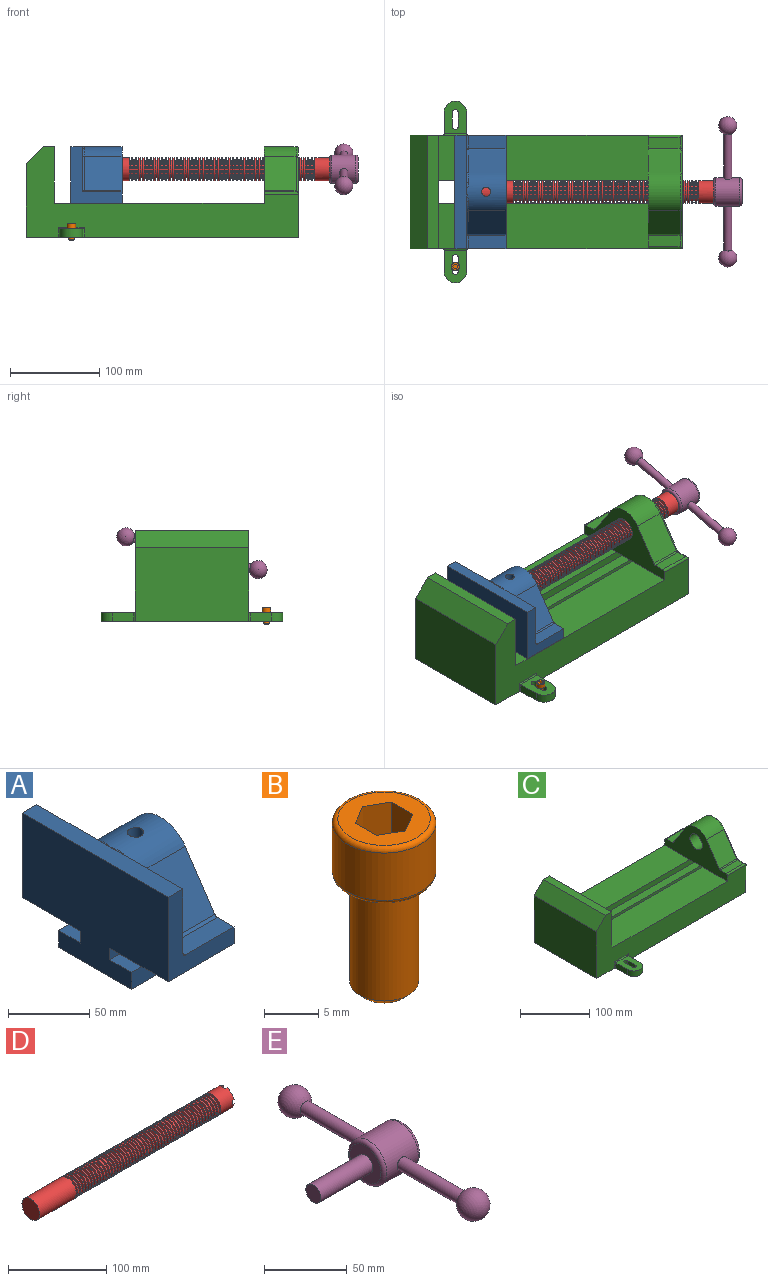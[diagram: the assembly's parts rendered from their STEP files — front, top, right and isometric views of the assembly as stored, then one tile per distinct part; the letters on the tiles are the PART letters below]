
ASSEMBLY  parts=5 mates=5
PART A: 36 faces, bbox 57.2x127x89 mm
  f0: plane 57.15x50.8mm, normal (0,0,-1), area 2903.2mm2, adj f6,f9,f10,f23
  f1: cylinder r=12.7mm len=44.45mm, axis (1,0,0), area 3464.3mm2, adj f6,f15,f16
  f2: plane 41.91x14.52mm, normal (0,0,1), area 608.5mm2, adj f6,f11,f24,f25
  f3: plane 51.86x48.26mm, normal (1,0,0), area 1495.7mm2, adj f8,f10,f31,f33,f35
  f4: plane 51.86x48.26mm, normal (1,0,0), area 1495.7mm2, adj f8,f11,f24,f28,f29
  f5: plane 57.15x50.8mm, normal (0,0,-1), area 2903.2mm2, adj f6,f9,f11,f22
  f6: plane 127x85.09mm, normal (1,0,0), area 5190.6mm2, adj f0,f1,f2,f5,f7,f10,f11,f12
  f7: plane 41.91x14.52mm, normal (0,0,1), area 608.5mm2, adj f6,f10,f30,f31
  f8: plane 127x12.7mm, normal (0,0,1), area 1612.9mm2, adj f3,f4,f9,f10,f11,f26,f34
  f9: plane 127x85.09mm, normal (-1,0,0), area 9096.8mm2, adj f0,f5,f8,f10,f11,f17,f18,f19
  f10: plane 63.5x57.15mm, normal (0,-1,0), area 1372.3mm2, adj f0,f3,f6,f7,f8,f9,f31
  f11: plane 63.5x57.15mm, normal (0,1,0), area 1372.3mm2, adj f2,f4,f5,f6,f8,f9,f24
  f12: plane 41.91x38.43mm, normal (0,-0.83,0.56), area 1939.2mm2, adj f6,f13,f30,f33
  f13: cylinder r=25.4mm len=44.45mm, axis (1,0,0), area 2026.5mm2, adj f6,f12,f14,f16,f26,f28,f34,f35
  f14: plane 41.91x38.43mm, normal (0,0.83,0.56), area 1939.2mm2, adj f6,f13,f25,f29
  f15: plane 25.4x25.4mm, normal (1,0,0), area 506.7mm2, adj f1
  f16: cylinder r=5.08mm len=13.76mm, axis (0,0,1), area 414mm2, adj f1,f13
  f17: plane 57.15x19.05mm, normal (0,0,1), area 1088.7mm2, adj f6,f9,f18,f23
  f18: plane 57.15x12.7mm, normal (0,-1,0), area 725.8mm2, adj f6,f9,f17,f19
  f19: plane 63.5x57.15mm, normal (0,0,-1), area 3629mm2, adj f6,f9,f18,f20
  f20: plane 57.15x12.7mm, normal (0,1,0), area 725.8mm2, adj f6,f9,f19,f21
  f21: plane 57.15x19.05mm, normal (0,0,1), area 1088.7mm2, adj f6,f9,f20,f22
  f22: plane 57.15x8.89mm, normal (0,1,0), area 508.1mm2, adj f5,f6,f9,f21
  f23: plane 57.15x8.89mm, normal (0,-1,0), area 508.1mm2, adj f0,f6,f9,f17
  f24: cylinder r=2.54mm len=14.52mm, axis (0,-1,0), area 57.9mm2, adj f2,f4,f11,f27
  f25: cylinder r=2.54mm len=41.91mm, axis (1,0,0), area 104.3mm2, adj f2,f6,f14,f27
  f26: bspline ~12.24x2.8mm, area 20.9mm2, adj f8,f13,f28
  f27: sphere r=2.54mm, area 6.3mm2, adj f24,f25,f29
  f28: torus R=27.94mm, axis (1,0,0), area 57.8mm2, adj f4,f13,f26,f29
  f29: cylinder r=2.54mm len=39.84mm, axis (0,-0.56,0.83), area 184.6mm2, adj f4,f14,f27,f28
  f30: cylinder r=2.54mm len=41.91mm, axis (1,0,0), area 104.3mm2, adj f6,f7,f12,f32
  f31: cylinder r=2.54mm len=14.52mm, axis (0,-1,0), area 57.9mm2, adj f3,f7,f10,f32
  f32: sphere r=2.54mm, area 6.3mm2, adj f30,f31,f33
  f33: cylinder r=2.54mm len=39.84mm, axis (0,-0.56,-0.83), area 184.6mm2, adj f3,f12,f32,f35
  f34: bspline ~12.24x2.8mm, area 20.9mm2, adj f8,f13,f35
  f35: torus R=27.94mm, axis (1,0,0), area 57.8mm2, adj f3,f13,f33,f34
PART B: 15 faces, bbox 10.3x10.3x19.1 mm
  f0: plane 8.51x8.51mm, normal (0,0,1), area 37.2mm2, adj f5,f6,f7,f8,f9,f10,f14
  f1: cylinder r=3.17mm len=11.94mm, axis (0,0,1), area 238.2mm2, adj f4,f12
  f2: plane 4.83x4.83mm, normal (0,0,-1), area 18.3mm2, adj f12
  f3: cylinder r=4.76mm len=9.53mm, axis (0,0,-1), area 159.6mm2, adj f13,f14
  f4: plane 8.51x8.51mm, normal (0,0,-1), area 25.2mm2, adj f1,f13
  f5: plane 4.83x2.38mm, normal (-0.5,-0.87,0), area 13.3mm2, adj f0,f6,f10,f11
  f6: plane 4.83x2.38mm, normal (0.5,-0.87,0), area 13.3mm2, adj f0,f5,f7,f11
  f7: plane 4.83x2.75mm, normal (1,0,0), area 13.3mm2, adj f0,f6,f8,f11
  f8: plane 4.83x2.38mm, normal (0.5,0.87,0), area 13.3mm2, adj f0,f7,f9,f11
  f9: plane 4.83x2.38mm, normal (-0.5,0.87,0), area 13.3mm2, adj f0,f8,f10,f11
  f10: plane 4.83x2.75mm, normal (-1,0,0), area 13.3mm2, adj f0,f5,f9,f11
  f11: plane 5.5x4.76mm, normal (0,0,1), area 19.6mm2, adj f5,f6,f7,f8,f9,f10
  f12: cone r=3.17mm half-angle=45deg, axis (0,0,1), area 18.9mm2, adj f1,f2
  f13: torus R=4.25mm, axis (0,0,1), area 23mm2, adj f3,f4
  f14: torus R=4.25mm, axis (0,0,1), area 23mm2, adj f0,f3
PART C: 61 faces, bbox 304.8x203.2x103.7 mm
  f0: plane 304.8x101.6mm, normal (0,1,0), area 13520.3mm2, adj f3,f4,f5,f6,f7,f8,f9,f16
  f1: plane 304.8x101.6mm, normal (0,-1,0), area 13520.3mm2, adj f2,f3,f5,f6,f7,f8,f9,f16
  f2: plane 234.95x50.8mm, normal (0,0,1), area 11935.5mm2, adj f1,f5,f16,f26
  f3: plane 127x99.06mm, normal (1,0,0), area 7097.5mm2, adj f0,f1,f9,f14,f17,f18,f19,f20
  f4: plane 234.95x50.8mm, normal (0,0,1), area 11935.5mm2, adj f0,f5,f16,f27
  f5: plane 127x101.6mm, normal (1,0,0), area 9516.1mm2, adj f0,f1,f2,f4,f6,f9,f18,f19
  f6: plane 127x12.7mm, normal (0,0,1), area 1612.9mm2, adj f0,f1,f5,f7
  f7: plane 127x19.05mm, normal (-0.71,0,0.71), area 3421.5mm2, adj f0,f1,f6,f8
  f8: plane 127x82.55mm, normal (-1,0,0), area 10483.8mm2, adj f0,f1,f7,f9
  f9: plane 304.8x203.2mm, normal (0,0,-1), area 33298.3mm2, adj f0,f1,f3,f5,f8,f21,f22,f39
  f10: plane 35.56x11.98mm, normal (0,0,1), area 426mm2, adj f16,f28,f29,f30
  f11: plane 38.43x35.56mm, normal (0,0.83,0.56), area 1645.4mm2, adj f12,f16,f29,f32
  f12: cylinder r=25.4mm len=42.19mm, axis (1,0,0), area 1770.2mm2, adj f11,f13,f16,f33
  f13: plane 38.43x35.56mm, normal (0,-0.83,0.56), area 1645.4mm2, adj f12,f16,f34,f35
  f14: cylinder r=12.7mm len=38.1mm, axis (1,0,0), area 3040.2mm2, adj f3,f16
  f15: plane 35.56x11.98mm, normal (0,0,1), area 426mm2, adj f16,f34,f36,f38
  f16: plane 127x63.5mm, normal (-1,0,0), area 4155.5mm2, adj f0,f1,f2,f4,f10,f11,f12,f13
  f17: plane 38.1x25.4mm, normal (0,0,-1), area 967.7mm2, adj f3,f16,f26,f27
  f18: plane 273.05x19.05mm, normal (0,0,-1), area 5201.6mm2, adj f3,f5,f19,f26
  f19: plane 273.05x12.7mm, normal (0,1,0), area 3467.7mm2, adj f3,f5,f18,f20
  f20: plane 273.05x19.05mm, normal (0,0,1), area 5201.6mm2, adj f3,f5,f19,f21
  f21: plane 273.05x16.51mm, normal (0,1,0), area 4508.1mm2, adj f3,f5,f9,f20
  f22: plane 273.05x16.51mm, normal (0,-1,0), area 4508.1mm2, adj f3,f5,f9,f23
  f23: plane 273.05x19.05mm, normal (0,0,1), area 5201.6mm2, adj f3,f5,f22,f24
  f24: plane 273.05x12.7mm, normal (0,-1,0), area 3467.7mm2, adj f3,f5,f23,f25
  f25: plane 273.05x19.05mm, normal (0,0,-1), area 5201.6mm2, adj f3,f5,f24,f27
  f26: plane 273.05x8.89mm, normal (0,1,0), area 2427.4mm2, adj f2,f3,f5,f17,f18
  f27: plane 273.05x8.89mm, normal (0,-1,0), area 2427.4mm2, adj f3,f4,f5,f17,f25
  f28: cylinder r=2.54mm len=38.1mm, axis (1,0,0), area 148.3mm2, adj f0,f10,f16,f30
  f29: cylinder r=2.54mm len=35.56mm, axis (-1,0,0), area 88.5mm2, adj f10,f11,f16,f31
  f30: cylinder r=2.54mm len=14.52mm, axis (0,1,0), area 54.3mm2, adj f3,f10,f28,f31
  f31: torus R=5.08mm, axis (-1,0,0), area 13.5mm2, adj f3,f29,f30,f32
  f32: cylinder r=2.54mm len=39.84mm, axis (0,0.56,-0.83), area 184.6mm2, adj f3,f11,f31,f33
  f33: torus R=22.86mm, axis (-1,0,0), area 191.4mm2, adj f3,f12,f32,f35
  f34: cylinder r=2.54mm len=35.56mm, axis (-1,0,0), area 88.5mm2, adj f13,f15,f16,f37
  f35: cylinder r=2.54mm len=39.84mm, axis (0,0.56,0.83), area 184.6mm2, adj f3,f13,f33,f37
  f36: cylinder r=2.54mm len=38.1mm, axis (-1,0,0), area 148.3mm2, adj f1,f15,f16,f38
  f37: torus R=5.08mm, axis (-1,0,0), area 13.5mm2, adj f3,f34,f35,f38
  f38: cylinder r=2.54mm len=14.52mm, axis (0,1,0), area 54.3mm2, adj f3,f15,f36,f37
  f39: plane 23.88x9.53mm, normal (-1,0,0), area 227.4mm2, adj f9,f45,f46,f60
  f40: plane 23.88x9.53mm, normal (1,0,0), area 227.4mm2, adj f9,f45,f46,f58
  f41: cylinder r=3.3mm len=9.53mm, axis (0,0,-1), area 98.8mm2, adj f9,f42,f44,f46
  f42: plane 15.62x9.53mm, normal (-1,0,0), area 148.8mm2, adj f9,f41,f43,f46
  f43: cylinder r=3.3mm len=9.53mm, axis (0,0,-1), area 98.8mm2, adj f9,f42,f44,f46
  f44: plane 15.62x9.53mm, normal (1,0,0), area 148.8mm2, adj f9,f41,f43,f46
  f45: cylinder r=12.7mm len=25.4mm, axis (0,0,-1), area 380mm2, adj f9,f39,f40,f46
  f46: plane 36.58x25.4mm, normal (0,0,1), area 722.4mm2, adj f39,f40,f41,f42,f43,f44,f45,f59
  f47: plane 23.88x9.53mm, normal (-1,0,0), area 227.4mm2, adj f9,f53,f54,f56
  f48: plane 23.88x9.53mm, normal (1,0,0), area 227.4mm2, adj f9,f53,f54,f55
  f49: cylinder r=3.3mm len=9.53mm, axis (0,0,-1), area 98.8mm2, adj f9,f50,f52,f54
  f50: plane 15.62x9.53mm, normal (-1,0,0), area 148.8mm2, adj f9,f49,f51,f54
  f51: cylinder r=3.3mm len=9.53mm, axis (0,0,-1), area 98.8mm2, adj f9,f50,f52,f54
  f52: plane 15.62x9.53mm, normal (1,0,0), area 148.8mm2, adj f9,f49,f51,f54
  f53: cylinder r=12.7mm len=25.4mm, axis (0,0,-1), area 380mm2, adj f9,f47,f48,f54
  f54: plane 36.58x25.4mm, normal (0,0,1), area 722.4mm2, adj f47,f48,f49,f50,f51,f52,f53,f57
  f55: cylinder r=1.52mm len=11.05mm, axis (0,0,-1), area 24.1mm2, adj f0,f9,f48,f57
  f56: cylinder r=1.52mm len=11.05mm, axis (0,0,1), area 24.1mm2, adj f0,f9,f47,f57
  f57: cylinder r=1.52mm len=28.45mm, axis (1,0,0), area 63.5mm2, adj f0,f54,f55,f56
  f58: cylinder r=1.52mm len=11.05mm, axis (0,0,1), area 24.1mm2, adj f1,f9,f40,f59
  f59: cylinder r=1.52mm len=28.45mm, axis (-1,0,0), area 63.5mm2, adj f1,f46,f58,f60
  f60: cylinder r=1.52mm len=11.05mm, axis (0,0,-1), area 24.1mm2, adj f1,f9,f39,f59
PART D: 220 faces, bbox 279.4x25.4x25.4 mm
  f0: cylinder r=12.7mm len=25.4mm, axis (-1,0,0), area 1468.2mm2, adj f1,f2,f3,f5,f7,f208,f209,f210
  f1: plane 9.9x9.9mm, normal (1,0,0), area 62.3mm2, adj f0,f4,f213,f216
  f2: plane 9.9x9.9mm, normal (1,0,0), area 62.3mm2, adj f0,f4,f210,f218
  f3: plane 9.9x9.9mm, normal (1,0,0), area 62.3mm2, adj f0,f4,f209,f212
  f4: cylinder r=6.35mm len=25.4mm, axis (1,0,0), area 960.3mm2, adj f1,f2,f3,f5,f6,f208,f209,f210
  f5: plane 9.9x9.9mm, normal (1,0,0), area 62.3mm2, adj f0,f4,f215,f217
  f6: plane 12.7x12.7mm, normal (1,0,0), area 126.7mm2, adj f4
  f7: cone r=12.7mm half-angle=76deg, axis (1,0,0), area 188mm2, adj f0,f9
  f8: cone r=10.16mm half-angle=76deg, axis (-1,0,0), area 188mm2, adj f9,f10
  f9: cylinder r=10.16mm len=20.32mm, axis (1,0,0), area 81.1mm2, adj f7,f8
  f10: cylinder r=12.7mm len=25.4mm, axis (-1,0,0), area 131.7mm2, adj f8,f11
  f11: cone r=12.7mm half-angle=76deg, axis (1,0,0), area 188mm2, adj f10,f13
  f12: cone r=10.16mm half-angle=76deg, axis (-1,0,0), area 188mm2, adj f13,f14
  f13: cylinder r=10.16mm len=20.32mm, axis (1,0,0), area 81.1mm2, adj f11,f12
  f14: cylinder r=12.7mm len=25.4mm, axis (-1,0,0), area 131.7mm2, adj f12,f15
  f15: cone r=12.7mm half-angle=76deg, axis (1,0,0), area 188mm2, adj f14,f17
  f16: cone r=10.16mm half-angle=76deg, axis (-1,0,0), area 188mm2, adj f17,f18
  f17: cylinder r=10.16mm len=20.32mm, axis (1,0,0), area 81.1mm2, adj f15,f16
  f18: cylinder r=12.7mm len=25.4mm, axis (-1,0,0), area 131.7mm2, adj f16,f19
  f19: cone r=12.7mm half-angle=76deg, axis (1,0,0), area 188mm2, adj f18,f21
  f20: cone r=10.16mm half-angle=76deg, axis (-1,0,0), area 188mm2, adj f21,f22
  f21: cylinder r=10.16mm len=20.32mm, axis (1,0,0), area 81.1mm2, adj f19,f20
  f22: cylinder r=12.7mm len=25.4mm, axis (-1,0,0), area 131.7mm2, adj f20,f23
  f23: cone r=12.7mm half-angle=76deg, axis (1,0,0), area 188mm2, adj f22,f25
  f24: cone r=10.16mm half-angle=76deg, axis (-1,0,0), area 188mm2, adj f25,f26
  f25: cylinder r=10.16mm len=20.32mm, axis (1,0,0), area 81.1mm2, adj f23,f24
  f26: cylinder r=12.7mm len=25.4mm, axis (-1,0,0), area 131.7mm2, adj f24,f27
  f27: cone r=12.7mm half-angle=76deg, axis (1,0,0), area 188mm2, adj f26,f29
  f28: cone r=10.16mm half-angle=76deg, axis (-1,0,0), area 188mm2, adj f29,f30
  f29: cylinder r=10.16mm len=20.32mm, axis (1,0,0), area 81.1mm2, adj f27,f28
  f30: cylinder r=12.7mm len=25.4mm, axis (-1,0,0), area 131.7mm2, adj f28,f31
  f31: cone r=12.7mm half-angle=76deg, axis (1,0,0), area 188mm2, adj f30,f33
  f32: cone r=10.16mm half-angle=76deg, axis (-1,0,0), area 188mm2, adj f33,f34
  f33: cylinder r=10.16mm len=20.32mm, axis (1,0,0), area 81.1mm2, adj f31,f32
  f34: cylinder r=12.7mm len=25.4mm, axis (-1,0,0), area 131.7mm2, adj f32,f35
  f35: cone r=12.7mm half-angle=76deg, axis (1,0,0), area 188mm2, adj f34,f37
  f36: cone r=10.16mm half-angle=76deg, axis (-1,0,0), area 188mm2, adj f37,f38
  f37: cylinder r=10.16mm len=20.32mm, axis (1,0,0), area 81.1mm2, adj f35,f36
  f38: cylinder r=12.7mm len=25.4mm, axis (-1,0,0), area 131.7mm2, adj f36,f39
  f39: cone r=12.7mm half-angle=76deg, axis (1,0,0), area 188mm2, adj f38,f41
  f40: cone r=10.16mm half-angle=76deg, axis (-1,0,0), area 188mm2, adj f41,f42
  f41: cylinder r=10.16mm len=20.32mm, axis (1,0,0), area 81.1mm2, adj f39,f40
  f42: cylinder r=12.7mm len=25.4mm, axis (-1,0,0), area 131.7mm2, adj f40,f43
  f43: cone r=12.7mm half-angle=76deg, axis (1,0,0), area 188mm2, adj f42,f45
  f44: cone r=10.16mm half-angle=76deg, axis (-1,0,0), area 188mm2, adj f45,f46
  f45: cylinder r=10.16mm len=20.32mm, axis (1,0,0), area 81.1mm2, adj f43,f44
  f46: cylinder r=12.7mm len=25.4mm, axis (-1,0,0), area 131.7mm2, adj f44,f47
  f47: cone r=12.7mm half-angle=76deg, axis (1,0,0), area 188mm2, adj f46,f49
  f48: cone r=10.16mm half-angle=76deg, axis (-1,0,0), area 188mm2, adj f49,f50
  f49: cylinder r=10.16mm len=20.32mm, axis (1,0,0), area 81.1mm2, adj f47,f48
  f50: cylinder r=12.7mm len=25.4mm, axis (-1,0,0), area 131.7mm2, adj f48,f51
  f51: cone r=12.7mm half-angle=76deg, axis (1,0,0), area 188mm2, adj f50,f53
  f52: cone r=10.16mm half-angle=76deg, axis (-1,0,0), area 188mm2, adj f53,f54
  f53: cylinder r=10.16mm len=20.32mm, axis (1,0,0), area 81.1mm2, adj f51,f52
  f54: cylinder r=12.7mm len=25.4mm, axis (-1,0,0), area 131.7mm2, adj f52,f55
  f55: cone r=12.7mm half-angle=76deg, axis (1,0,0), area 188mm2, adj f54,f57
  f56: cone r=10.16mm half-angle=76deg, axis (-1,0,0), area 188mm2, adj f57,f58
  f57: cylinder r=10.16mm len=20.32mm, axis (1,0,0), area 81.1mm2, adj f55,f56
  f58: cylinder r=12.7mm len=25.4mm, axis (-1,0,0), area 131.7mm2, adj f56,f59
  f59: cone r=12.7mm half-angle=76deg, axis (1,0,0), area 188mm2, adj f58,f61
  f60: cone r=10.16mm half-angle=76deg, axis (-1,0,0), area 188mm2, adj f61,f62
  f61: cylinder r=10.16mm len=20.32mm, axis (1,0,0), area 81.1mm2, adj f59,f60
  f62: cylinder r=12.7mm len=25.4mm, axis (-1,0,0), area 131.7mm2, adj f60,f63
  f63: cone r=12.7mm half-angle=76deg, axis (1,0,0), area 188mm2, adj f62,f65
  f64: cone r=10.16mm half-angle=76deg, axis (-1,0,0), area 188mm2, adj f65,f66
  f65: cylinder r=10.16mm len=20.32mm, axis (1,0,0), area 81.1mm2, adj f63,f64
  f66: cylinder r=12.7mm len=25.4mm, axis (-1,0,0), area 131.7mm2, adj f64,f67
  f67: cone r=12.7mm half-angle=76deg, axis (1,0,0), area 188mm2, adj f66,f69
  f68: cone r=10.16mm half-angle=76deg, axis (-1,0,0), area 188mm2, adj f69,f70
  f69: cylinder r=10.16mm len=20.32mm, axis (1,0,0), area 81.1mm2, adj f67,f68
  f70: cylinder r=12.7mm len=25.4mm, axis (-1,0,0), area 131.7mm2, adj f68,f71
  f71: cone r=12.7mm half-angle=76deg, axis (1,0,0), area 188mm2, adj f70,f73
  f72: cone r=10.16mm half-angle=76deg, axis (-1,0,0), area 188mm2, adj f73,f74
  f73: cylinder r=10.16mm len=20.32mm, axis (1,0,0), area 81.1mm2, adj f71,f72
  f74: cylinder r=12.7mm len=25.4mm, axis (-1,0,0), area 131.7mm2, adj f72,f75
  f75: cone r=12.7mm half-angle=76deg, axis (1,0,0), area 188mm2, adj f74,f77
  f76: cone r=10.16mm half-angle=76deg, axis (-1,0,0), area 188mm2, adj f77,f78
  f77: cylinder r=10.16mm len=20.32mm, axis (1,0,0), area 81.1mm2, adj f75,f76
  f78: cylinder r=12.7mm len=25.4mm, axis (-1,0,0), area 131.7mm2, adj f76,f79
  f79: cone r=12.7mm half-angle=76deg, axis (1,0,0), area 188mm2, adj f78,f81
  f80: cone r=10.16mm half-angle=76deg, axis (-1,0,0), area 188mm2, adj f81,f82
  f81: cylinder r=10.16mm len=20.32mm, axis (1,0,0), area 81.1mm2, adj f79,f80
  f82: cylinder r=12.7mm len=25.4mm, axis (-1,0,0), area 131.7mm2, adj f80,f83
  f83: cone r=12.7mm half-angle=76deg, axis (1,0,0), area 188mm2, adj f82,f85
  f84: cone r=10.16mm half-angle=76deg, axis (-1,0,0), area 188mm2, adj f85,f86
  f85: cylinder r=10.16mm len=20.32mm, axis (1,0,0), area 81.1mm2, adj f83,f84
  f86: cylinder r=12.7mm len=25.4mm, axis (-1,0,0), area 131.7mm2, adj f84,f87
  f87: cone r=12.7mm half-angle=76deg, axis (1,0,0), area 188mm2, adj f86,f89
  f88: cone r=10.16mm half-angle=76deg, axis (-1,0,0), area 188mm2, adj f89,f90
  f89: cylinder r=10.16mm len=20.32mm, axis (1,0,0), area 81.1mm2, adj f87,f88
  f90: cylinder r=12.7mm len=25.4mm, axis (-1,0,0), area 131.7mm2, adj f88,f91
  f91: cone r=12.7mm half-angle=76deg, axis (1,0,0), area 188mm2, adj f90,f93
  f92: cone r=10.16mm half-angle=76deg, axis (-1,0,0), area 188mm2, adj f93,f94
  f93: cylinder r=10.16mm len=20.32mm, axis (1,0,0), area 81.1mm2, adj f91,f92
  f94: cylinder r=12.7mm len=25.4mm, axis (-1,0,0), area 131.7mm2, adj f92,f95
  f95: cone r=12.7mm half-angle=76deg, axis (1,0,0), area 188mm2, adj f94,f97
  f96: cone r=10.16mm half-angle=76deg, axis (-1,0,0), area 188mm2, adj f97,f98
  f97: cylinder r=10.16mm len=20.32mm, axis (1,0,0), area 81.1mm2, adj f95,f96
  f98: cylinder r=12.7mm len=25.4mm, axis (-1,0,0), area 131.7mm2, adj f96,f99
  f99: cone r=12.7mm half-angle=76deg, axis (1,0,0), area 188mm2, adj f98,f101
  f100: cone r=10.16mm half-angle=76deg, axis (-1,0,0), area 188mm2, adj f101,f102
  f101: cylinder r=10.16mm len=20.32mm, axis (1,0,0), area 81.1mm2, adj f99,f100
  f102: cylinder r=12.7mm len=25.4mm, axis (-1,0,0), area 131.7mm2, adj f100,f103
  f103: cone r=12.7mm half-angle=76deg, axis (1,0,0), area 188mm2, adj f102,f105
  f104: cone r=10.16mm half-angle=76deg, axis (-1,0,0), area 188mm2, adj f105,f106
  f105: cylinder r=10.16mm len=20.32mm, axis (1,0,0), area 81.1mm2, adj f103,f104
  f106: cylinder r=12.7mm len=25.4mm, axis (-1,0,0), area 131.7mm2, adj f104,f107
  f107: cone r=12.7mm half-angle=76deg, axis (1,0,0), area 188mm2, adj f106,f109
  f108: cone r=10.16mm half-angle=76deg, axis (-1,0,0), area 188mm2, adj f109,f110
  f109: cylinder r=10.16mm len=20.32mm, axis (1,0,0), area 81.1mm2, adj f107,f108
  f110: cylinder r=12.7mm len=25.4mm, axis (-1,0,0), area 131.7mm2, adj f108,f111
  f111: cone r=12.7mm half-angle=76deg, axis (1,0,0), area 188mm2, adj f110,f113
  f112: cone r=10.16mm half-angle=76deg, axis (-1,0,0), area 188mm2, adj f113,f114
  f113: cylinder r=10.16mm len=20.32mm, axis (1,0,0), area 81.1mm2, adj f111,f112
  f114: cylinder r=12.7mm len=25.4mm, axis (-1,0,0), area 131.7mm2, adj f112,f115
  f115: cone r=12.7mm half-angle=76deg, axis (1,0,0), area 188mm2, adj f114,f117
  f116: cone r=10.16mm half-angle=76deg, axis (-1,0,0), area 188mm2, adj f117,f118
  f117: cylinder r=10.16mm len=20.32mm, axis (1,0,0), area 81.1mm2, adj f115,f116
  f118: cylinder r=12.7mm len=25.4mm, axis (-1,0,0), area 131.7mm2, adj f116,f119
  f119: cone r=12.7mm half-angle=76deg, axis (1,0,0), area 188mm2, adj f118,f121
  f120: cone r=10.16mm half-angle=76deg, axis (-1,0,0), area 188mm2, adj f121,f122
  f121: cylinder r=10.16mm len=20.32mm, axis (1,0,0), area 81.1mm2, adj f119,f120
  f122: cylinder r=12.7mm len=25.4mm, axis (-1,0,0), area 131.7mm2, adj f120,f123
  f123: cone r=12.7mm half-angle=76deg, axis (1,0,0), area 188mm2, adj f122,f125
  f124: cone r=10.16mm half-angle=76deg, axis (-1,0,0), area 188mm2, adj f125,f126
  f125: cylinder r=10.16mm len=20.32mm, axis (1,0,0), area 81.1mm2, adj f123,f124
  f126: cylinder r=12.7mm len=25.4mm, axis (-1,0,0), area 131.7mm2, adj f124,f127
  f127: cone r=12.7mm half-angle=76deg, axis (1,0,0), area 188mm2, adj f126,f129
  f128: cone r=10.16mm half-angle=76deg, axis (-1,0,0), area 188mm2, adj f129,f130
  f129: cylinder r=10.16mm len=20.32mm, axis (1,0,0), area 81.1mm2, adj f127,f128
  f130: cylinder r=12.7mm len=25.4mm, axis (-1,0,0), area 131.7mm2, adj f128,f131
  f131: cone r=12.7mm half-angle=76deg, axis (1,0,0), area 188mm2, adj f130,f133
  f132: cone r=10.16mm half-angle=76deg, axis (-1,0,0), area 188mm2, adj f133,f134
  f133: cylinder r=10.16mm len=20.32mm, axis (1,0,0), area 81.1mm2, adj f131,f132
  f134: cylinder r=12.7mm len=25.4mm, axis (-1,0,0), area 131.7mm2, adj f132,f135
  f135: cone r=12.7mm half-angle=76deg, axis (1,0,0), area 188mm2, adj f134,f137
  f136: cone r=10.16mm half-angle=76deg, axis (-1,0,0), area 188mm2, adj f137,f138
  f137: cylinder r=10.16mm len=20.32mm, axis (1,0,0), area 81.1mm2, adj f135,f136
  f138: cylinder r=12.7mm len=25.4mm, axis (-1,0,0), area 131.7mm2, adj f136,f139
  f139: cone r=12.7mm half-angle=76deg, axis (1,0,0), area 188mm2, adj f138,f141
  f140: cone r=10.16mm half-angle=76deg, axis (-1,0,0), area 188mm2, adj f141,f142
  f141: cylinder r=10.16mm len=20.32mm, axis (1,0,0), area 81.1mm2, adj f139,f140
  f142: cylinder r=12.7mm len=25.4mm, axis (-1,0,0), area 131.7mm2, adj f140,f143
  f143: cone r=12.7mm half-angle=76deg, axis (1,0,0), area 188mm2, adj f142,f145
  f144: cone r=10.16mm half-angle=76deg, axis (-1,0,0), area 188mm2, adj f145,f146
  f145: cylinder r=10.16mm len=20.32mm, axis (1,0,0), area 81.1mm2, adj f143,f144
  f146: cylinder r=12.7mm len=25.4mm, axis (-1,0,0), area 131.7mm2, adj f144,f147
  f147: cone r=12.7mm half-angle=76deg, axis (1,0,0), area 188mm2, adj f146,f149
  f148: cone r=10.16mm half-angle=76deg, axis (-1,0,0), area 188mm2, adj f149,f150
  f149: cylinder r=10.16mm len=20.32mm, axis (1,0,0), area 81.1mm2, adj f147,f148
  f150: cylinder r=12.7mm len=25.4mm, axis (-1,0,0), area 131.7mm2, adj f148,f151
  f151: cone r=12.7mm half-angle=76deg, axis (1,0,0), area 188mm2, adj f150,f153
  f152: cone r=10.16mm half-angle=76deg, axis (-1,0,0), area 188mm2, adj f153,f154
  f153: cylinder r=10.16mm len=20.32mm, axis (1,0,0), area 81.1mm2, adj f151,f152
  f154: cylinder r=12.7mm len=25.4mm, axis (-1,0,0), area 131.7mm2, adj f152,f155
  f155: cone r=12.7mm half-angle=76deg, axis (1,0,0), area 188mm2, adj f154,f157
  f156: cone r=10.16mm half-angle=76deg, axis (-1,0,0), area 188mm2, adj f157,f158
  f157: cylinder r=10.16mm len=20.32mm, axis (1,0,0), area 81.1mm2, adj f155,f156
  f158: cylinder r=12.7mm len=25.4mm, axis (-1,0,0), area 131.7mm2, adj f156,f159
  f159: cone r=12.7mm half-angle=76deg, axis (1,0,0), area 188mm2, adj f158,f161
  f160: cone r=10.16mm half-angle=76deg, axis (-1,0,0), area 188mm2, adj f161,f162
  f161: cylinder r=10.16mm len=20.32mm, axis (1,0,0), area 81.1mm2, adj f159,f160
  f162: cylinder r=12.7mm len=25.4mm, axis (-1,0,0), area 131.7mm2, adj f160,f163
  f163: cone r=12.7mm half-angle=76deg, axis (1,0,0), area 188mm2, adj f162,f165
  f164: cone r=10.16mm half-angle=76deg, axis (-1,0,0), area 188mm2, adj f165,f166
  f165: cylinder r=10.16mm len=20.32mm, axis (1,0,0), area 81.1mm2, adj f163,f164
  f166: cylinder r=12.7mm len=25.4mm, axis (-1,0,0), area 131.7mm2, adj f164,f167
  f167: cone r=12.7mm half-angle=76deg, axis (1,0,0), area 188mm2, adj f166,f169
  f168: cone r=10.16mm half-angle=76deg, axis (-1,0,0), area 188mm2, adj f169,f170
  f169: cylinder r=10.16mm len=20.32mm, axis (1,0,0), area 81.1mm2, adj f167,f168
  f170: cylinder r=12.7mm len=25.4mm, axis (-1,0,0), area 131.7mm2, adj f168,f171
  f171: cone r=12.7mm half-angle=76deg, axis (1,0,0), area 188mm2, adj f170,f173
  f172: cone r=10.16mm half-angle=76deg, axis (-1,0,0), area 188mm2, adj f173,f174
  f173: cylinder r=10.16mm len=20.32mm, axis (1,0,0), area 81.1mm2, adj f171,f172
  f174: cylinder r=12.7mm len=25.4mm, axis (-1,0,0), area 131.7mm2, adj f172,f175
  f175: cone r=12.7mm half-angle=76deg, axis (1,0,0), area 188mm2, adj f174,f177
  f176: cone r=10.16mm half-angle=76deg, axis (-1,0,0), area 188mm2, adj f177,f178
  f177: cylinder r=10.16mm len=20.32mm, axis (1,0,0), area 81.1mm2, adj f175,f176
  f178: cylinder r=12.7mm len=25.4mm, axis (-1,0,0), area 131.7mm2, adj f176,f179
  f179: cone r=12.7mm half-angle=76deg, axis (1,0,0), area 188mm2, adj f178,f181
  f180: cone r=10.16mm half-angle=76deg, axis (-1,0,0), area 188mm2, adj f181,f182
  f181: cylinder r=10.16mm len=20.32mm, axis (1,0,0), area 81.1mm2, adj f179,f180
  f182: cylinder r=12.7mm len=25.4mm, axis (-1,0,0), area 131.7mm2, adj f180,f183
  f183: cone r=12.7mm half-angle=76deg, axis (1,0,0), area 188mm2, adj f182,f185
  f184: cone r=10.16mm half-angle=76deg, axis (-1,0,0), area 188mm2, adj f185,f186
  f185: cylinder r=10.16mm len=20.32mm, axis (1,0,0), area 81.1mm2, adj f183,f184
  f186: cylinder r=12.7mm len=25.4mm, axis (-1,0,0), area 131.7mm2, adj f184,f187
  f187: cone r=12.7mm half-angle=76deg, axis (1,0,0), area 188mm2, adj f186,f189
  f188: cone r=10.16mm half-angle=76deg, axis (-1,0,0), area 188mm2, adj f189,f190
  f189: cylinder r=10.16mm len=20.32mm, axis (1,0,0), area 81.1mm2, adj f187,f188
  f190: cylinder r=12.7mm len=25.4mm, axis (-1,0,0), area 131.7mm2, adj f188,f191
  f191: cone r=12.7mm half-angle=76deg, axis (1,0,0), area 188mm2, adj f190,f193
  f192: cone r=10.16mm half-angle=76deg, axis (-1,0,0), area 188mm2, adj f193,f194
  f193: cylinder r=10.16mm len=20.32mm, axis (1,0,0), area 81.1mm2, adj f191,f192
  f194: cylinder r=12.7mm len=25.4mm, axis (-1,0,0), area 131.7mm2, adj f192,f195
  f195: cone r=12.7mm half-angle=76deg, axis (1,0,0), area 188mm2, adj f194,f197
  f196: cone r=10.16mm half-angle=76deg, axis (-1,0,0), area 188mm2, adj f197,f198
  f197: cylinder r=10.16mm len=20.32mm, axis (1,0,0), area 81.1mm2, adj f195,f196
  f198: cylinder r=12.7mm len=25.4mm, axis (-1,0,0), area 131.7mm2, adj f196,f199
  f199: cone r=12.7mm half-angle=76deg, axis (1,0,0), area 188mm2, adj f198,f201
  f200: cone r=10.16mm half-angle=76deg, axis (-1,0,0), area 188mm2, adj f201,f202
  f201: cylinder r=10.16mm len=20.32mm, axis (1,0,0), area 81.1mm2, adj f199,f200
  f202: cylinder r=12.7mm len=25.4mm, axis (-1,0,0), area 131.7mm2, adj f200,f203
  f203: cone r=12.7mm half-angle=76deg, axis (1,0,0), area 188mm2, adj f202,f205
  f204: cone r=10.16mm half-angle=76deg, axis (-1,0,0), area 188mm2, adj f205,f207
  f205: cylinder r=10.16mm len=20.32mm, axis (1,0,0), area 81.1mm2, adj f203,f204
  f206: plane 25.4x25.4mm, normal (-1,0,0), area 506.7mm2, adj f207
  f207: cylinder r=12.7mm len=52.45mm, axis (-1,0,0), area 4185.4mm2, adj f204,f206
  f208: plane 6.88x5.08mm, normal (1,0,0), area 32.7mm2, adj f0,f4,f209,f210
  f209: plane 6.62x2.54mm, normal (0,-1,0), area 16.8mm2, adj f0,f3,f4,f208
  f210: plane 6.62x2.54mm, normal (0,1,0), area 16.8mm2, adj f0,f2,f4,f208
  f211: plane 6.88x5.08mm, normal (1,0,0), area 32.7mm2, adj f0,f4,f212,f213
  f212: plane 6.62x2.54mm, normal (0,0,1), area 16.8mm2, adj f0,f3,f4,f211
  f213: plane 6.62x2.54mm, normal (0,0,-1), area 16.8mm2, adj f0,f1,f4,f211
  f214: plane 6.88x5.08mm, normal (1,0,0), area 32.7mm2, adj f0,f4,f215,f216
  f215: plane 6.62x2.54mm, normal (0,1,0), area 16.8mm2, adj f0,f4,f5,f214
  f216: plane 6.62x2.54mm, normal (0,-1,0), area 16.8mm2, adj f0,f1,f4,f214
  f217: plane 6.62x2.54mm, normal (0,0,-1), area 16.8mm2, adj f0,f4,f5,f219
  f218: plane 6.62x2.54mm, normal (0,0,1), area 16.8mm2, adj f0,f2,f4,f219
  f219: plane 6.88x5.08mm, normal (1,0,0), area 32.7mm2, adj f0,f4,f217,f218
PART E: 11 faces, bbox 76.2x172.7x34.4 mm
  f0: sphere r=10.16mm, area 1231.8mm2, adj f1
  f1: cylinder r=4.45mm len=51.82mm, axis (0,1,0), area 1438.5mm2, adj f0,f4
  f2: sphere r=10.16mm, area 1231.8mm2, adj f3
  f3: cylinder r=4.45mm len=51.82mm, axis (0,1,0), area 1438.5mm2, adj f2,f4
  f4: cylinder r=15.88mm len=31.75mm, axis (-1,0,0), area 2534.7mm2, adj f1,f3,f9,f10
  f5: cylinder r=6.35mm len=44.45mm, axis (-1,0,0), area 1773.5mm2, adj f6,f8
  f6: plane 12.7x12.7mm, normal (-1,0,0), area 126.7mm2, adj f5
  f7: plane 26.67x26.67mm, normal (1,0,0), area 558.6mm2, adj f10
  f8: plane 26.67x26.67mm, normal (-1,0,0), area 432mm2, adj f5,f9
  f9: torus R=13.33mm, axis (1,0,0), area 374.8mm2, adj f4,f8
  f10: torus R=13.33mm, axis (1,0,0), area 374.8mm2, adj f4,f7
PLACE A t=(18.56,0,0)mm
PLACE B rot(axis=(0,0,1),153.6deg) t=(-254,-83.45,9.52)mm
PLACE C at identity fixed
PLACE D rot(axis=(1,0,0),13.9deg) t=(18.56,18.26,2.22)mm
PLACE E rot(axis=(1,0,0),13.9deg) t=(-3.03,18.26,2.22)mm
MATE fastened D.f4 <-> E.f5  axis (1,0,0) through (35.07,0,76.2)mm
MATE planar A.f0 <-> C.f2  axis (0,0,-1) through (-225.91,-38.1,38.1)mm
MATE pin_slot B.f1 <-> C.f41  axis (0,0,1) through (-254,-83.45,9.52)mm
MATE revolute D.f7 <-> A.f28  axis (-1,0,0) through (-241.79,0,76.2)mm
MATE cylindrical C.f12 <-> D.f7  axis (-1,0,0) through (-38.1,0,76.2)mm
